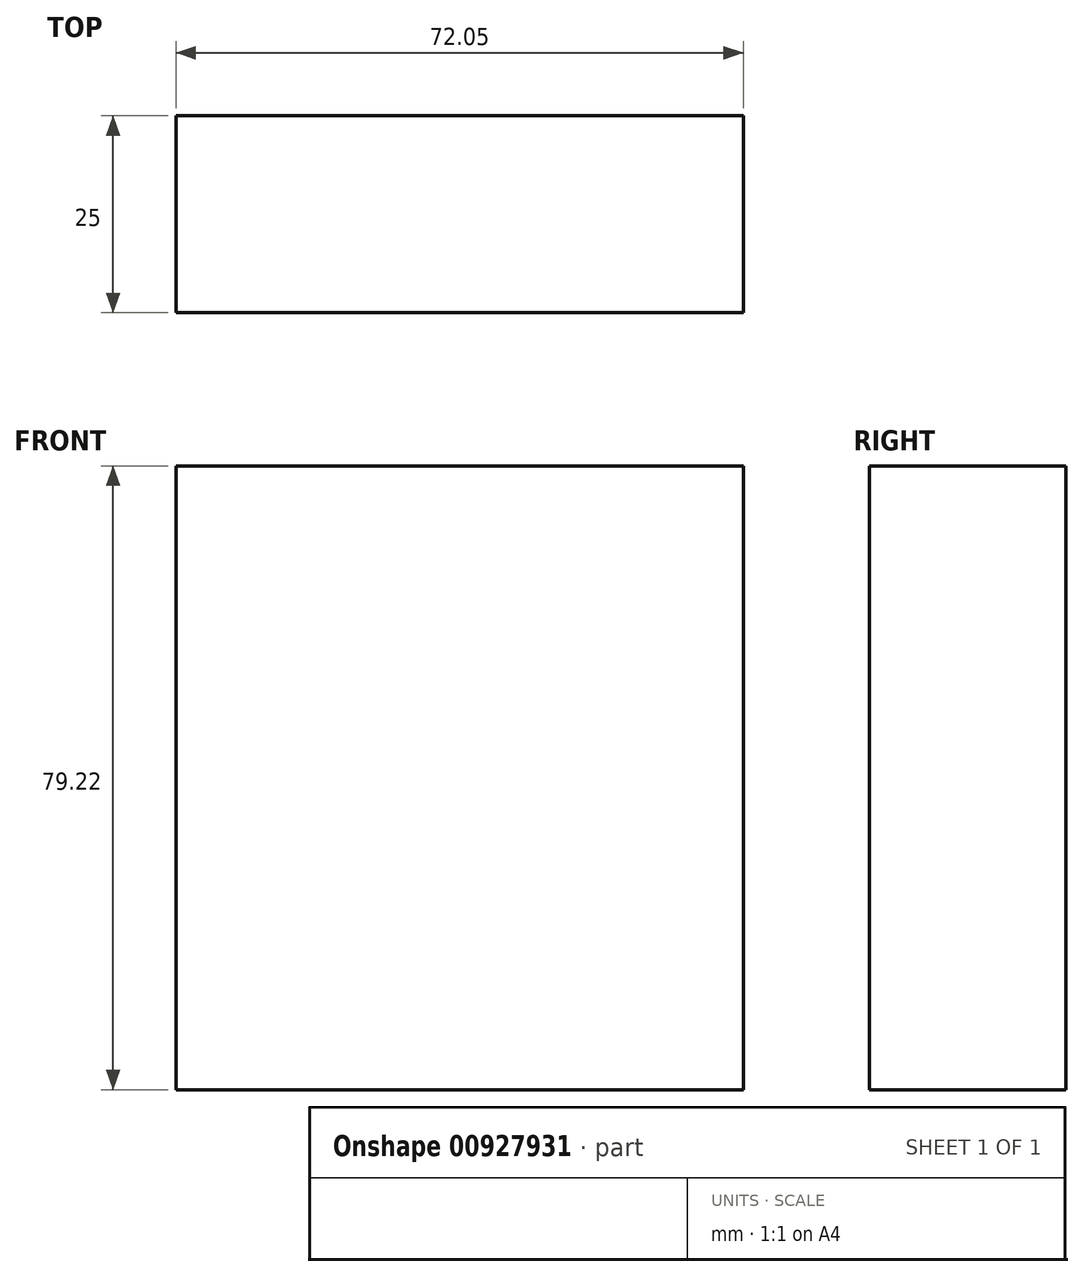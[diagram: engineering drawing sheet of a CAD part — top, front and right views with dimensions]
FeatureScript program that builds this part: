
annotation { "Feature Type Name" : "Feature", "Feature Type Description" : "" }
export const myFeature = defineFeature(function(context is Context, id is Id, definition is map)
    precondition{}
    {
        {
            var Q0;
            Q0=qCreatedBy(makeId("Front.planeOp"),FACE);
            var sketch = newSketch(context, id + "F0", { "sketchPlane" : qUnion([Q0])});
            skLineSegment(sketch, "E0.bottom", {"start": v(-113.43, -21.55) * mm, "end": v(-41.38, -21.55) * mm});
            skLineSegment(sketch, "E0.top", {"start": v(-113.43, 57.67) * mm, "end": v(-41.38, 57.67) * mm});
            skLineSegment(sketch, "E0.left", {"start": v(-113.43, -21.55) * mm, "end": v(-113.43, 57.67) * mm});
            skLineSegment(sketch, "E0.right", {"start": v(-41.38, -21.55) * mm, "end": v(-41.38, 57.67) * mm});
            skPoint(sketch, "E0.middle", {"position": v(-77.4, 18.06) * mm});
            skSolve(sketch);
        }
        {
            var Q0;
            Q0=makeQuery(id+"F0.imprint","IMPRINT",FACE,{"disambiguationData":[TD([[makeQuery(id+"F0.imprint","IMPRINT",EDGE,{"derivedFrom":sQuery(id+"F0.wireOp",EDGE,"E0.bottom")}),1.0]])]});
            extrude(context, id + "F1", {"entities" : qUnion([Q0]), "depth" : 25 * mm, "offsetDistance" : 25 * mm});
        }
    });
